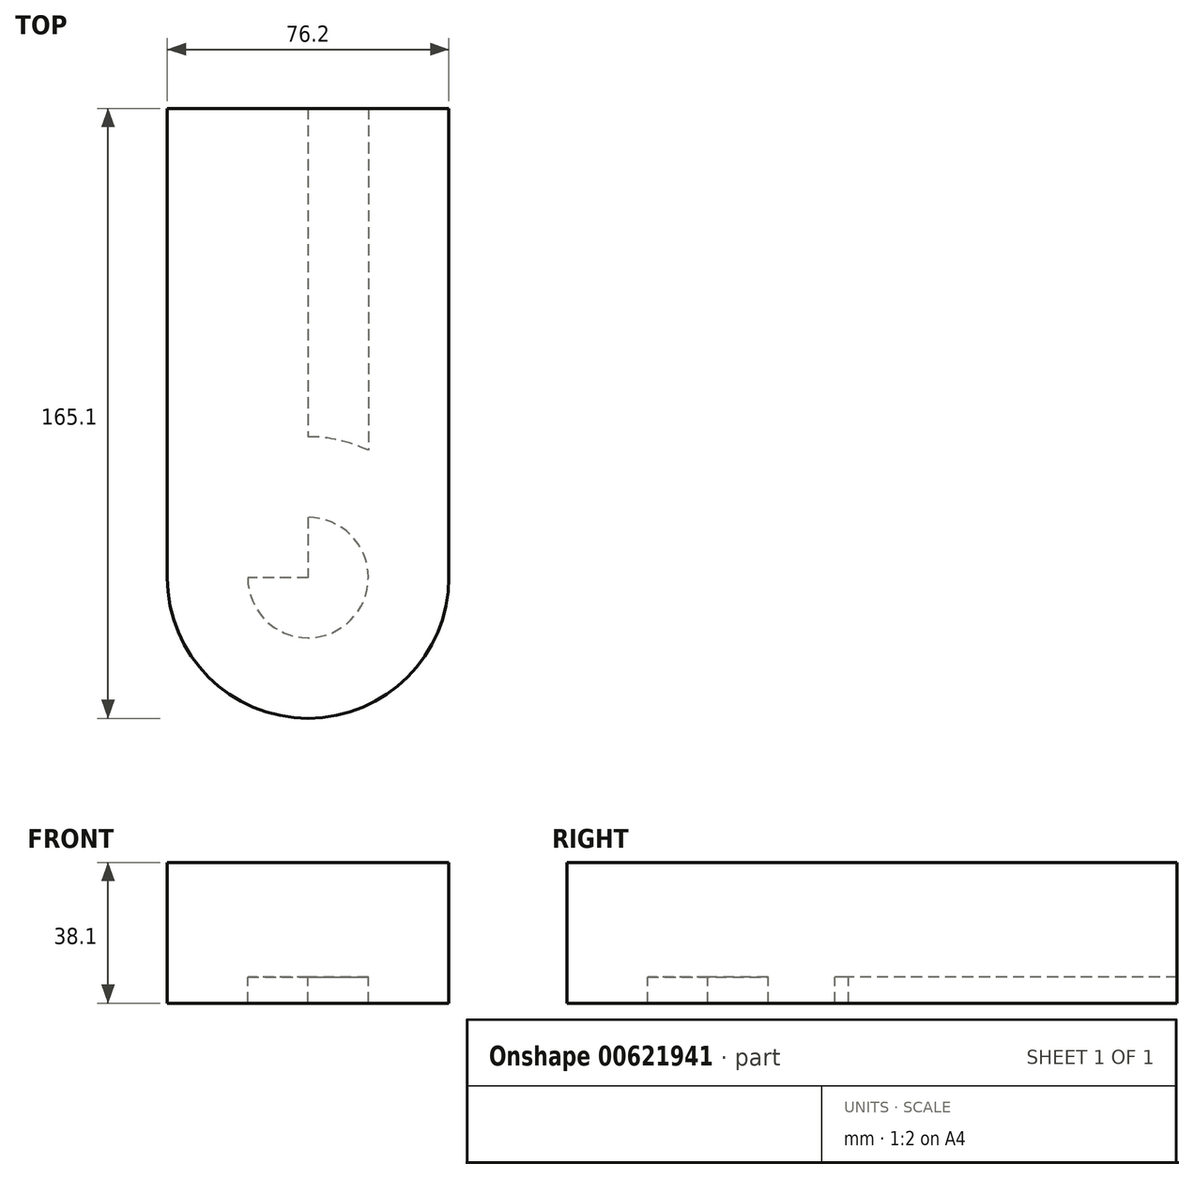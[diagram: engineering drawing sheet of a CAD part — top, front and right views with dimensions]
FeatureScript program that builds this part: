
annotation { "Feature Type Name" : "Feature", "Feature Type Description" : "" }
export const myFeature = defineFeature(function(context is Context, id is Id, definition is map)
    precondition{}
    {
        {
            var Q0;
            Q0=qCreatedBy(makeId("Front.planeOp"),FACE);
            var sketch = newSketch(context, id + "F0", { "sketchPlane" : qUnion([Q0])});
            skLineSegment(sketch, "E0.bottom", {"start": v(-38.1, -19.05) * mm, "end": v(38.1, -19.05) * mm});
            skLineSegment(sketch, "E0.top", {"start": v(-38.1, 19.05) * mm, "end": v(38.1, 19.05) * mm});
            skLineSegment(sketch, "E0.left", {"start": v(-38.1, -19.05) * mm, "end": v(-38.1, 19.05) * mm});
            skLineSegment(sketch, "E0.right", {"start": v(38.1, -19.05) * mm, "end": v(38.1, 19.05) * mm});
            skPoint(sketch, "E0.middle", {"position": v(0, 0) * mm});
            skLineSegment(sketch, "E1.bottom", {"start": v(105.07, 69.28) * mm, "end": v(54.27, 69.28) * mm});
            skLineSegment(sketch, "E1.top", {"start": v(105.07, 43.88) * mm, "end": v(54.27, 43.88) * mm});
            skLineSegment(sketch, "E1.left", {"start": v(105.07, 69.28) * mm, "end": v(105.07, 43.88) * mm});
            skLineSegment(sketch, "E1.right", {"start": v(54.27, 69.28) * mm, "end": v(54.27, 43.88) * mm});
            skPoint(sketch, "E1.middle", {"position": v(79.67, 56.58) * mm});
            skLineSegment(sketch, "E2", {"start": v(38.1, 19.05) * mm, "end": v(38.1, 33.58) * mm});
            skArc(sketch, "E3", {"start": v(50.8, 46.28) * mm, "mid": v(41.82, 42.56) * mm, "end": v(38.1, 33.58) * mm});
            skLineSegment(sketch, "E4", {"start": v(50.8, 46.28) * mm, "end": v(54.27, 46.28) * mm});
            skLineSegment(sketch, "E5.0", {"start": v(50.8, 55.68) * mm, "end": v(55.59, 55.68) * mm});
            skArc(sketch, "E5.1", {"start": v(50.8, 55.68) * mm, "mid": v(35.17, 49.2) * mm, "end": v(28.7, 33.58) * mm});
            skLineSegment(sketch, "E5.2", {"start": v(28.7, 15.92) * mm, "end": v(28.7, 33.58) * mm});
            skFitSpline(sketch, "E6", {"points": [v(54.27, 69.28) * mm, v(16.03, 58.15) * mm, v(-28.01, 38.74) * mm, v(-38.1, 19.05) * mm], "startDerivative": vector(-101.64, -28.8) * mm, "endDerivative": vector(-21.66, -79.55) * mm});
            skSolve(sketch);
        }
        {
            var Q0;
            Q0=makeQuery(id+"F0.imprint","IMPRINT",FACE,{"disambiguationData":[TD([[makeQuery(id+"F0.imprint","IMPRINT",EDGE,{"derivedFrom":sQuery(id+"F0.wireOp",EDGE,"E0.bottom")}),1.0]])]});
            extrude(context, id + "F1", {"entities" : qUnion([Q0]), "endBound" : BoundingType.SYMMETRIC, "depth" : 127 * mm, "offsetDistance" : 25.4 * mm});
        }
        {
            var Q0;
            {var subQ0=sQuery(id+"F0.wireOp",EDGE,"E2");Q0=makeQuery(id+"F0.imprint","IMPRINT",FACE,{"disambiguationData":[TD([[makeQuery(id+"F0.imprint","IMPRINT",EDGE,{"derivedFrom":subQ0}),1.0]])]});}
            extrude(context, id + "F2", {"entities" : qUnion([Q0]), "operationType" : NewBodyOperationType.ADD, "endBound" : BoundingType.SYMMETRIC, "depth" : 50.8 * mm, "offsetDistance" : 25.4 * mm});
        }
        {
            var Q0;
            {var subQ0=sQuery(id+"F0.wireOp",EDGE,"E5.1");Q0=makeQuery(id+"F0.imprint","IMPRINT",FACE,{"disambiguationData":[TD([[makeQuery(id+"F0.imprint","IMPRINT",EDGE,{"derivedFrom":subQ0}),-1.0]])]});}
            extrude(context, id + "F3", {"entities" : qUnion([Q0]), "operationType" : NewBodyOperationType.ADD, "endBound" : BoundingType.SYMMETRIC, "depth" : 25.4 * mm, "offsetDistance" : 25.4 * mm});
        }
        {
            var Q0;
            {var subQ1=sQuery(id+"F0.wireOp",EDGE,"E1.bottom");Q0=makeQuery(id+"F0.imprint","IMPRINT",FACE,{"disambiguationData":[TD([[makeQuery(id+"F0.imprint","IMPRINT",EDGE,{"derivedFrom":subQ1}),1.0]])]});}
            extrude(context, id + "F4", {"entities" : qUnion([Q0]), "endBound" : BoundingType.SYMMETRIC, "depth" : 50.8 * mm, "offsetDistance" : 25.4 * mm});
        }
        {
            var Q0;
            Q0=makeQuery(id+"F4.opExtrude","CAP_FACE",FACE,{"disambiguationData":[OSD([sQuery(id+"F0.wireOp",EDGE,"E1.bottom"),sQuery(id+"F0.wireOp",EDGE,"E1.top"),sQuery(id+"F0.wireOp",EDGE,"E1.left"),sQuery(id+"F0.wireOp",EDGE,"E1.right")])],"isStart":true});
            var Q1;
            Q1=sQuery(id+"F0.wireOp",EDGE,"E1.left");
            revolve(context, id + "F5", {"entities" : qUnion([Q0]), "axis" : qUnion([Q1]), "revolveType" : RevolveType.FULL});
        }
        {
            var Q0;
            Q0=makeQuery(id+"F1.opExtrude","CAP_FACE",FACE,{"disambiguationData":[OSD([sQuery(id+"F0.wireOp",EDGE,"E0.bottom"),sQuery(id+"F0.wireOp",EDGE,"E0.top"),sQuery(id+"F0.wireOp",EDGE,"E0.left"),sQuery(id+"F0.wireOp",EDGE,"E0.right")])],"isStart":false});
            var sketch = newSketch(context, id + "F6", { "sketchPlane" : qUnion([Q0])});
            skPoint(sketch, "E7", {"position": v(0, -19.05) * mm});
            skLineSegment(sketch, "E8.bottom", {"start": v(0, -19.05) * mm, "end": v(16.3, -19.05) * mm});
            skLineSegment(sketch, "E8.top", {"start": v(0, -12.02) * mm, "end": v(16.3, -12.02) * mm});
            skLineSegment(sketch, "E8.left", {"start": v(0, -19.05) * mm, "end": v(0, -12.02) * mm});
            skLineSegment(sketch, "E8.right", {"start": v(16.3, -19.05) * mm, "end": v(16.3, -12.02) * mm});
            skSolve(sketch);
        }
        {
            var Q0;
            Q0=makeQuery(id+"F6.imprint","IMPRINT",FACE,{"disambiguationData":[TD([[makeQuery(id+"F6.imprint","IMPRINT",EDGE,{"derivedFrom":sQuery(id+"F6.wireOp",EDGE,"E8.top")}),1.0]])]});
            extrude(context, id + "F7", {"entities" : qUnion([Q0]), "operationType" : NewBodyOperationType.INTERSECT, "endBound" : BoundingType.THROUGH_ALL, "oppositeDirection" : true, "depth" : 25.4 * mm, "offsetDistance" : 25.4 * mm});
        }
        {
            var Q0;
            Q0=makeQuery(id+"F5.opRevolve","SWEPT_FACE",FACE,{"disambiguationData":[OSD([sQuery(id+"F0.wireOp",EDGE,"E1.bottom")])]});
            var sketch = newSketch(context, id + "F8", { "sketchPlane" : qUnion([Q0])});
            skSolve(sketch);
        }
        {
            var Q0;
            Q0=makeQuery(id+"F1.opExtrude","CAP_FACE",FACE,{"disambiguationData":[OSD([sQuery(id+"F0.wireOp",EDGE,"E0.bottom"),sQuery(id+"F0.wireOp",EDGE,"E0.top"),sQuery(id+"F0.wireOp",EDGE,"E0.left"),sQuery(id+"F0.wireOp",EDGE,"E0.right")])],"isStart":false});
            var sketch = newSketch(context, id + "F9", { "sketchPlane" : qUnion([Q0])});
            skLineSegment(sketch, "E9", {"start": v(0, 19.05) * mm, "end": v(0, -12.02) * mm});
            skSolve(sketch);
        }
        {
            var Q0;
            {var subQ3=sQuery(id+"F9.wireOp",EDGE,"E9");Q0=makeQuery(id+"F9.imprint","IMPRINT",FACE,{"disambiguationData":[TD([[makeQuery(id+"F9.imprint","IMPRINT",EDGE,{"derivedFrom":subQ3}),1.0]])]});}
            var Q1;
            Q1=sQuery(id+"F9.wireOp",EDGE,"E9");
            revolve(context, id + "F10", {"operationType" : NewBodyOperationType.ADD, "entities" : qUnion([Q0]), "axis" : qUnion([Q1]), "revolveType" : RevolveType.FULL});
        }
    });
